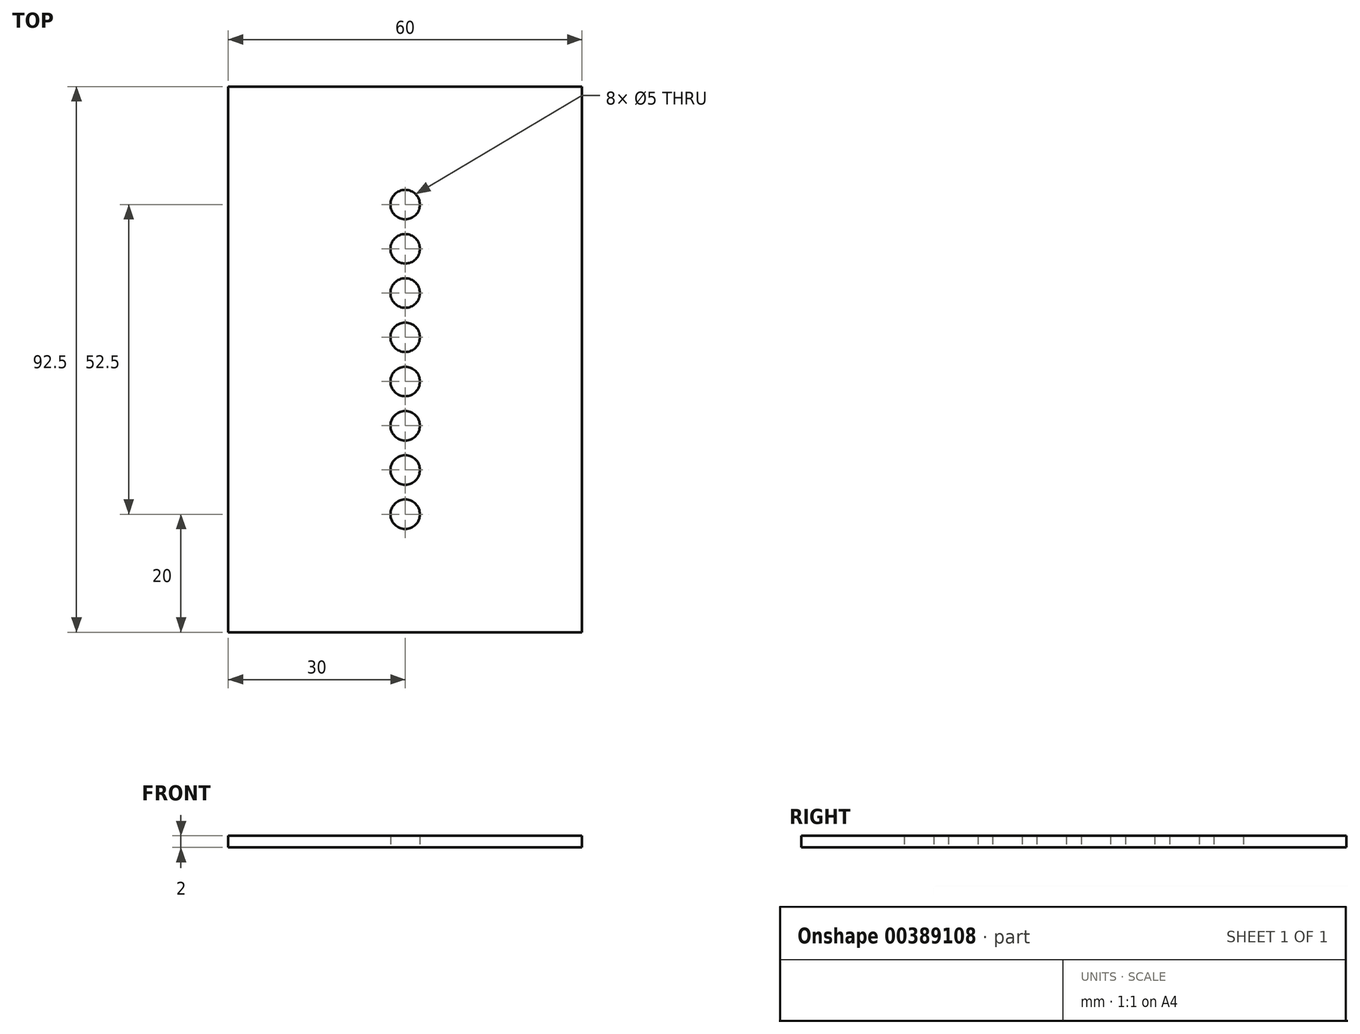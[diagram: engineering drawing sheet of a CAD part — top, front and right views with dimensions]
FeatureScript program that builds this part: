
annotation { "Feature Type Name" : "Feature", "Feature Type Description" : "" }
export const myFeature = defineFeature(function(context is Context, id is Id, definition is map)
    precondition{}
    {
        {
            var Q0;
            Q0=qCreatedBy(makeId("Top.planeOp"),FACE);
            var sketch = newSketch(context, id + "F0", { "sketchPlane" : qUnion([Q0])});
            skCircle(sketch, "E0", {"center": v(0, 0) * mm, "radius": 2.5 * mm});
            skCircle(sketch, "E1.0.1.0", {"center": v(0, -7.5) * mm, "radius": 2.5 * mm});
            skCircle(sketch, "E1.0.2.0", {"center": v(0, -15) * mm, "radius": 2.5 * mm});
            skCircle(sketch, "E1.0.3.0", {"center": v(0, -22.5) * mm, "radius": 2.5 * mm});
            skCircle(sketch, "E1.0.4.0", {"center": v(0, -30) * mm, "radius": 2.5 * mm});
            skLineSegment(sketch, "E1.direction1", {"start": v(0, 0) * mm, "end": v(14.3, 0) * mm, "construction": true});
            skLineSegment(sketch, "E1.direction2", {"start": v(0, 0) * mm, "end": v(0, -7.5) * mm, "construction": true});
            skCircle(sketch, "E2.0.0.5", {"center": v(0, -37.5) * mm, "radius": 2.5 * mm});
            skCircle(sketch, "E2.0.0.6", {"center": v(0, -45) * mm, "radius": 2.5 * mm});
            skCircle(sketch, "E2.0.0.7", {"center": v(0, -52.5) * mm, "radius": 2.5 * mm});
            skLineSegment(sketch, "E3.bottom", {"start": v(-30, 20) * mm, "end": v(30, 20) * mm});
            skLineSegment(sketch, "E3.top", {"start": v(-30, -72.5) * mm, "end": v(30, -72.5) * mm});
            skLineSegment(sketch, "E3.left", {"start": v(-30, 20) * mm, "end": v(-30, -72.5) * mm});
            skLineSegment(sketch, "E3.right", {"start": v(30, 20) * mm, "end": v(30, -72.5) * mm});
            skSolve(sketch);
        }
        {
            var Q0;
            Q0=makeQuery(id+"F0.imprint","IMPRINT",FACE,{"disambiguationData":[TD([[makeQuery(id+"F0.imprint","IMPRINT",EDGE,{"derivedFrom":sQuery(id+"F0.wireOp",EDGE,"E0")}),-1.0]])]});
            extrude(context, id + "F1", {"entities" : qUnion([Q0]), "depth" : 2 * mm});
        }
    });
